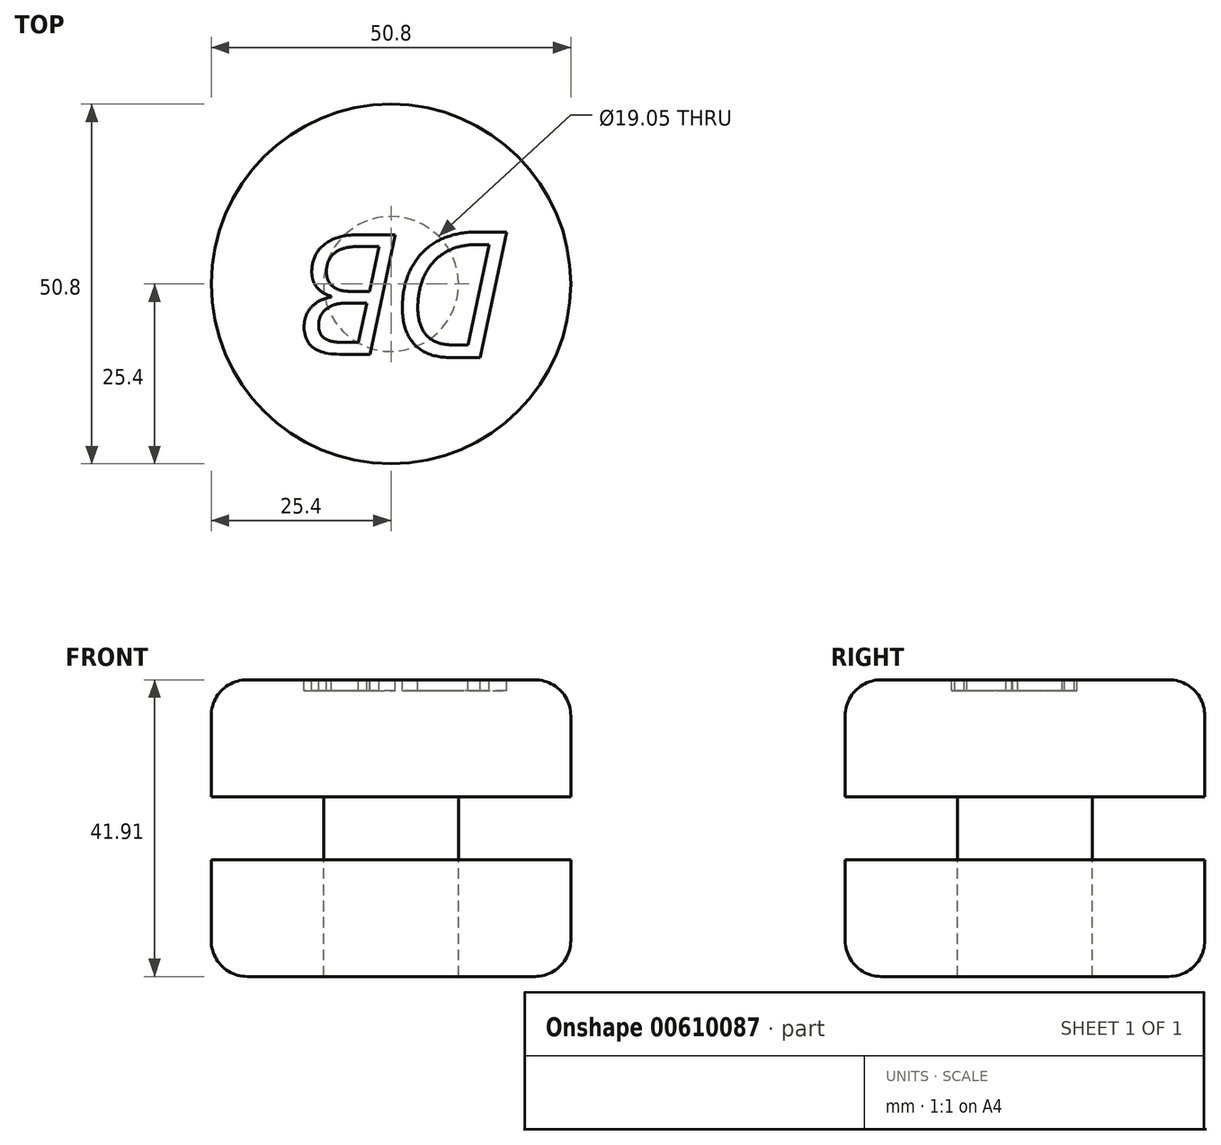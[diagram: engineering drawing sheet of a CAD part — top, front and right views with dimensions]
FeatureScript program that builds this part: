
annotation { "Feature Type Name" : "Feature", "Feature Type Description" : "" }
export const myFeature = defineFeature(function(context is Context, id is Id, definition is map)
    precondition{}
    {
        {
            var Q0;
            Q0=qCreatedBy(makeId("Top.planeOp"),FACE);
            var sketch = newSketch(context, id + "F0", { "sketchPlane" : qUnion([Q0])});
            skCircle(sketch, "E0", {"center": v(0, 0) * mm, "radius": 25.4 * mm});
            skSolve(sketch);
        }
        {
            var Q0;
            Q0=makeQuery(id+"F0.imprint","IMPRINT",FACE,{"disambiguationData":[TD([[makeQuery(id+"F0.imprint","IMPRINT",EDGE,{"derivedFrom":sQuery(id+"F0.wireOp",EDGE,"E0")}),1.0]])]});
            extrude(context, id + "F1", {"entities" : qUnion([Q0]), "depth" : 16.5 * mm, "offsetDistance" : 25.4 * mm});
        }
        {
            var Q0;
            Q0=makeQuery(id+"F1.opExtrude","CAP_FACE",FACE,{"disambiguationData":[OSD([sQuery(id+"F0.wireOp",EDGE,"E0")])],"isStart":false});
            fillet(context, id + "F2", {"entities" : qUnion([Q0]), "radius" : 5.08 * mm, "tangentPropagation" : true, "allowEdgeOverflow" : false});
        }
        {
            var Q0;
            Q0=makeQuery(id+"F1.opExtrude","CAP_FACE",FACE,{"disambiguationData":[OSD([sQuery(id+"F0.wireOp",EDGE,"E0")])],"isStart":true});
            var sketch = newSketch(context, id + "F3", { "sketchPlane" : qUnion([Q0])});
            skSolve(sketch);
        }
        {
            var Q0;
            Q0=makeQuery(id+"F3.imprint","IMPRINT",FACE,{"disambiguationData":[TD([[makeQuery(id+"F3.imprint","IMPRINT",EDGE,{"derivedFrom":makeQuery(id+"F1.opExtrude","CAP_EDGE",EDGE,{"disambiguationData":[OSD([sQuery(id+"F0.wireOp",EDGE,"E0")])],"isStart":true})}),-1.0]])]});
            var sketch = newSketch(context, id + "F4", { "sketchPlane" : qUnion([Q0])});
            skCircle(sketch, "E1", {"center": v(0, 0) * mm, "radius": 9.53 * mm});
            skSolve(sketch);
        }
        {
            var Q0;
            Q0=makeQuery(id+"F4.imprint","IMPRINT",FACE,{"disambiguationData":[TD([[makeQuery(id+"F4.imprint","IMPRINT",EDGE,{"derivedFrom":sQuery(id+"F4.wireOp",EDGE,"E1")}),1.0]])]});
            extrude(context, id + "F5", {"entities" : qUnion([Q0]), "operationType" : NewBodyOperationType.ADD, "depth" : 8.9 * mm, "offsetDistance" : 25.4 * mm});
        }
        {
            var Q0;
            Q0=makeQuery(id+"F5.opExtrude","CAP_FACE",FACE,{"disambiguationData":[OSD([sQuery(id+"F4.wireOp",EDGE,"E1")])],"isStart":false});
            var sketch = newSketch(context, id + "F6", { "sketchPlane" : qUnion([Q0])});
            skCircle(sketch, "E2", {"center": v(0, 0) * mm, "radius": 25.4 * mm});
            skSolve(sketch);
        }
        {
            var Q0;
            Q0=makeQuery(id+"F6.imprint","IMPRINT",FACE,{"disambiguationData":[TD([[makeQuery(id+"F6.imprint","IMPRINT",EDGE,{"derivedFrom":sQuery(id+"F6.wireOp",EDGE,"E2")}),1.0]])]});
            extrude(context, id + "F7", {"entities" : qUnion([Q0]), "depth" : 12.7 * mm, "offsetDistance" : 25.4 * mm});
        }
        {
            var Q0;
            Q0=makeQuery(id+"F7.opExtrude","CAP_FACE",FACE,{"disambiguationData":[OSD([sQuery(id+"F4.wireOp",EDGE,"E1"),sQuery(id+"F6.wireOp",EDGE,"E2")])],"isStart":false});
            var sketch = newSketch(context, id + "F8", { "sketchPlane" : qUnion([Q0])});
            skCircle(sketch, "E3", {"center": v(0, 0) * mm, "radius": 25.4 * mm});
            skSolve(sketch);
        }
        {
            var Q0;
            Q0=makeQuery(id+"F8.imprint","IMPRINT",FACE,{"disambiguationData":[TD([[makeQuery(id+"F8.imprint","IMPRINT",EDGE,{"derivedFrom":sQuery(id+"F8.wireOp",EDGE,"E3")}),1.0]])]});
            extrude(context, id + "F9", {"entities" : qUnion([Q0]), "operationType" : NewBodyOperationType.ADD, "depth" : 3.8 * mm, "offsetDistance" : 25.4 * mm});
        }
        {
            var Q0;
            Q0=makeQuery(id+"F9.opExtrude","CAP_EDGE",EDGE,{"disambiguationData":[OSD([sQuery(id+"F8.wireOp",EDGE,"E3")])],"isStart":false});
            fillet(context, id + "F10", {"entities" : qUnion([Q0]), "radius" : 5.08 * mm, "tangentPropagation" : true, "allowEdgeOverflow" : false});
        }
        {
            var Q0;
            Q0=makeQuery(id+"F5.opExtrude","CAP_FACE",FACE,{"disambiguationData":[OSD([sQuery(id+"F4.wireOp",EDGE,"E1")])],"isStart":false});
            var sketch = newSketch(context, id + "F11", { "sketchPlane" : qUnion([Q0])});
            skCircle(sketch, "E4", {"center": v(0, 0) * mm, "radius": 9.53 * mm});
            skSolve(sketch);
        }
        {
            var Q0;
            Q0=makeQuery(id+"F11.imprint","IMPRINT",FACE,{"disambiguationData":[TD([[makeQuery(id+"F11.imprint","IMPRINT",EDGE,{"derivedFrom":sQuery(id+"F11.wireOp",EDGE,"E4")}),1.0]])]});
            extrude(context, id + "F12", {"entities" : qUnion([Q0]), "depth" : 16.5 * mm, "offsetDistance" : 25.4 * mm});
        }
        {
            var Q0;
            Q0=makeQuery(id+"F1.opExtrude","CAP_FACE",FACE,{"disambiguationData":[OSD([sQuery(id+"F0.wireOp",EDGE,"E0")])],"isStart":false});
            var sketch = newSketch(context, id + "F13", { "sketchPlane" : qUnion([Q0])});
            skText(sketch, "E5", { "text": "D", "fontName": "OpenSans-Italic.ttf"});
            const initialGuessF13  = {"E5": [0.01737, 0.00733, -1, 0, 0.01787]};
            skSetInitialGuess(sketch, initialGuessF13);
            skSolve(sketch);
        }
        {
            var Q0;
            Q0 = qSketchRegion(id + "F13", true);
            extrude(context, id + "F14", {"entities" : qUnion([Q0]), "operationType" : NewBodyOperationType.REMOVE, "oppositeDirection" : true, "depth" : 1.52 * mm, "offsetDistance" : 25.4 * mm});
        }
        {
            var Q0;
            {var subQ0=sQuery(id+"F0.wireOp",EDGE,"E0");Q0=makeQuery(id+"F14.boolean.opBoolean","SPLIT",FACE,{"disambiguationData":[TD([makeQuery(id+"F2.opFillet","BLEND_FACE",FACE,{"disambiguationData":[OSD([subQ0])]})])],"derivedFrom":makeQuery(id+"F1.opExtrude","CAP_FACE",FACE,{"disambiguationData":[OSD([subQ0])],"isStart":false})});}
            var sketch = newSketch(context, id + "F15", { "sketchPlane" : qUnion([Q0])});
            skText(sketch, "E6", { "text": "B", "fontName": "OpenSans-Italic.ttf"});
            const initialGuessF15  = {"E6": [0.0016, 0.00695, -1, 0, 0.01702]};
            skSetInitialGuess(sketch, initialGuessF15);
            skSolve(sketch);
        }
        {
            var Q0;
            Q0 = qSketchRegion(id + "F15", true);
            extrude(context, id + "F16", {"entities" : qUnion([Q0]), "operationType" : NewBodyOperationType.REMOVE, "oppositeDirection" : true, "depth" : 1.52 * mm, "offsetDistance" : 25.4 * mm});
        }
    });
